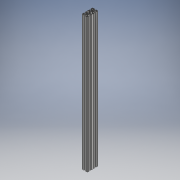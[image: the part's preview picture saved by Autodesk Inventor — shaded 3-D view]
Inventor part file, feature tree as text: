
AUTODESK INVENTOR PART (.ipt)
format: ipt  version: 2018 (Build 220112000, 112)  size: 628,736 bytes
history: native  units: mm
features: other x1, extrude x1, sketch x1
ambient origin geometry x8: Origin, YZ Plane, XZ Plane, XY Plane, X Axis, Y Axis, Z Axis, Center Point
bodies: Body1 (feature_tree)
feature tree (3):
  other  "Sólido1"
  extrude  "Extrusão1"  [1 undecoded]
  sketch  "Esboço1"  dims[d0=1000.0mm d1=0.0mm]
note: 1 required parameter value undecoded (feature->parameter linkage not recoverable at this tier; creation-order binding heuristic only, values carry confidence <= 0.55)
